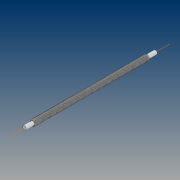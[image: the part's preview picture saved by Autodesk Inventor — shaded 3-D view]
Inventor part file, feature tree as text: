
AUTODESK INVENTOR PART (.ipt)
format: ipt  version: 2021 (Build 250183000, 183)  size: 669,184 bytes
history: native  units: mm
features: sketch x2, revolve x1, helix x1, projected_geometry x1
ambient origin geometry x8: Origin, YZ Plane, XZ Plane, XY Plane, X Axis, Y Axis, Z Axis, Center Point
bodies: Solid1 (feature_tree)
feature tree (5):
  revolve  "Revolution1"  [1 undecoded]
  helix  "Coil1"  [1 undecoded]
  sketch  "Sketch1"  dims[d0=4.0mm d1=19.4mm d2=300.0mm]
  sketch  "Sketch2"  dims[d3=5.0mm d4=90.0deg d5=261.2mm d6=60.0deg d7=1.5mm d8=2.0mm d9=261.2mm d10=10.0mm d11=0.0mm d12=90.0deg d13=90.0deg d14=0.0mm d15=0.0mm]
  projected_geometry  "Projected Loop1"
note: 2 required parameter values undecoded (feature->parameter linkage not recoverable at this tier; creation-order binding heuristic only, values carry confidence <= 0.55)